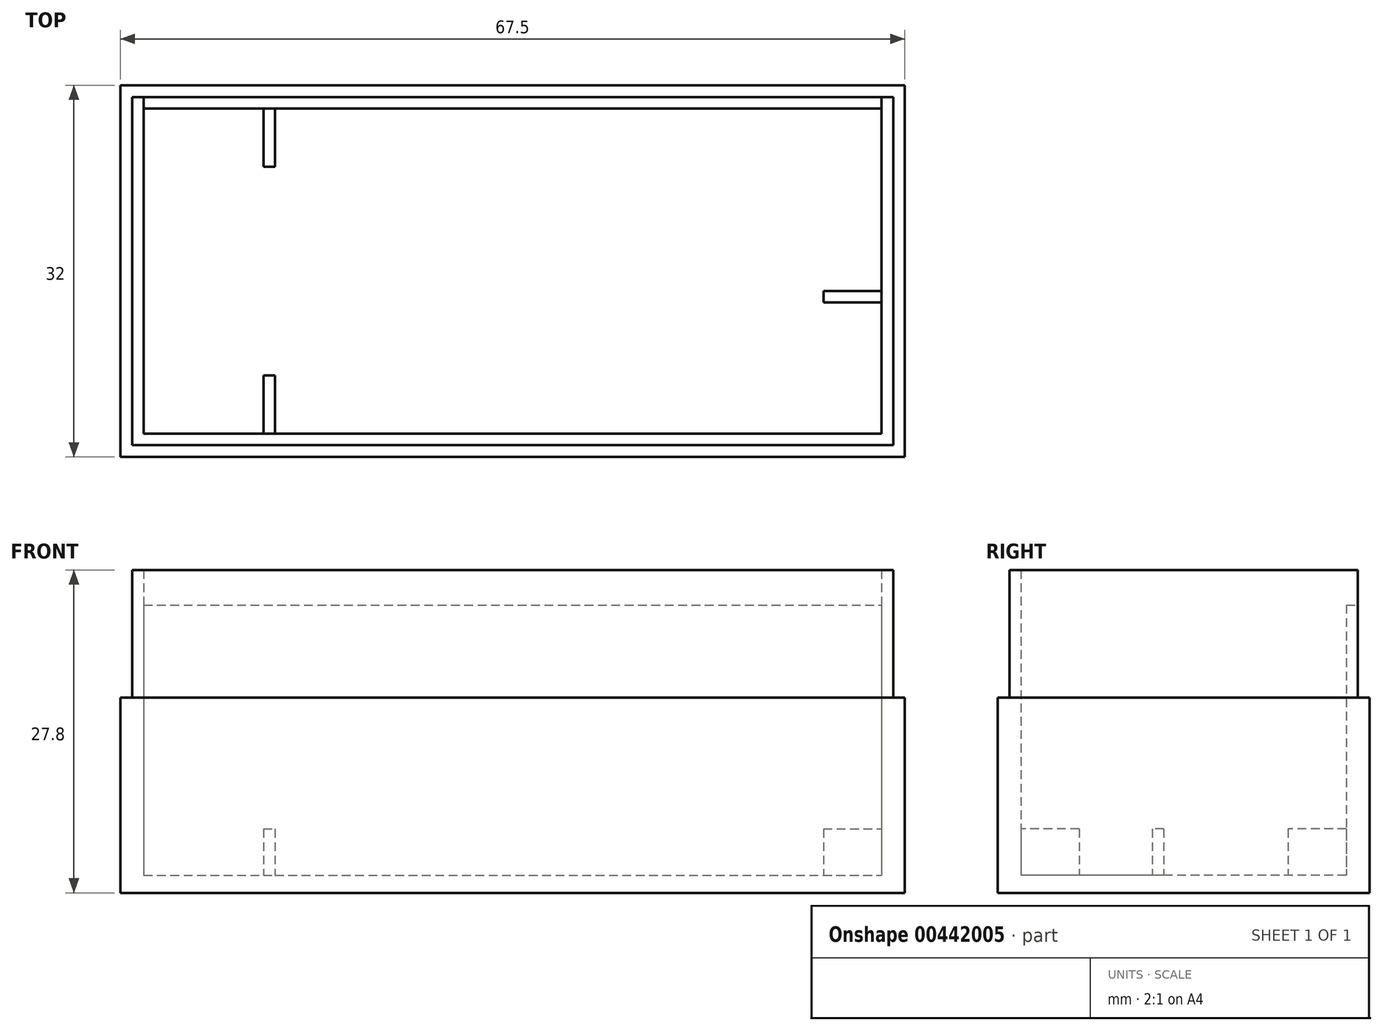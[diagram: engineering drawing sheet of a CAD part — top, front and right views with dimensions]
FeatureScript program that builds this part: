
annotation { "Feature Type Name" : "Feature", "Feature Type Description" : "" }
export const myFeature = defineFeature(function(context is Context, id is Id, definition is map)
    precondition{}
    {
        {
            var Q0;
            Q0=qCreatedBy(makeId("Top.planeOp"),FACE);
            var sketch = newSketch(context, id + "F0", { "sketchPlane" : qUnion([Q0])});
            skLineSegment(sketch, "E0.bottom", {"start": v(0, 0) * mm, "end": v(67.5, 0) * mm});
            skLineSegment(sketch, "E0.top", {"start": v(0, 32) * mm, "end": v(67.5, 32) * mm});
            skLineSegment(sketch, "E0.left", {"start": v(0, 0) * mm, "end": v(0, 32) * mm});
            skLineSegment(sketch, "E0.right", {"start": v(67.5, 0) * mm, "end": v(67.5, 32) * mm});
            skSolve(sketch);
        }
        {
            var Q0;
            Q0 = qSketchRegion(id + "F0", true);
            extrude(context, id + "F1", {"entities" : qUnion([Q0]), "depth" : 1.5 * mm});
        }
        {
            var Q0;
            Q0=makeQuery(id+"F1.opExtrude","CAP_FACE",FACE,{"disambiguationData":[OSD([sQuery(id+"F0.wireOp",EDGE,"E0.bottom"),sQuery(id+"F0.wireOp",EDGE,"E0.top"),sQuery(id+"F0.wireOp",EDGE,"E0.left"),sQuery(id+"F0.wireOp",EDGE,"E0.right")])],"isStart":false});
            var sketch = newSketch(context, id + "F2", { "sketchPlane" : qUnion([Q0])});
            skLineSegment(sketch, "E1.bottom", {"start": v(0, 32) * mm, "end": v(67.5, 32) * mm});
            skLineSegment(sketch, "E1.top", {"start": v(0, 0) * mm, "end": v(67.5, 0) * mm});
            skLineSegment(sketch, "E1.left", {"start": v(0, 32) * mm, "end": v(0, 0) * mm});
            skLineSegment(sketch, "E1.right", {"start": v(67.5, 32) * mm, "end": v(67.5, 0) * mm});
            skLineSegment(sketch, "E2.bottom", {"start": v(2, 30) * mm, "end": v(65.5, 30) * mm});
            skLineSegment(sketch, "E2.top", {"start": v(2, 2) * mm, "end": v(65.5, 2) * mm});
            skLineSegment(sketch, "E2.left", {"start": v(2, 30) * mm, "end": v(2, 2) * mm});
            skLineSegment(sketch, "E2.right", {"start": v(65.5, 30) * mm, "end": v(65.5, 2) * mm});
            skSolve(sketch);
        }
        {
            var Q0;
            Q0 = qSketchRegion(id + "F2", true);
            extrude(context, id + "F3", {"entities" : qUnion([Q0]), "operationType" : NewBodyOperationType.ADD, "depth" : 26.3 * mm});
        }
        {
            var Q0;
            Q0=makeQuery(id+"F3.opExtrude","CAP_FACE",FACE,{"disambiguationData":[OSD([sQuery(id+"F2.wireOp",EDGE,"E1.bottom"),sQuery(id+"F2.wireOp",EDGE,"E1.top"),sQuery(id+"F2.wireOp",EDGE,"E1.left"),sQuery(id+"F2.wireOp",EDGE,"E1.right"),sQuery(id+"F2.wireOp",EDGE,"E2.bottom"),sQuery(id+"F2.wireOp",EDGE,"E2.top"),sQuery(id+"F2.wireOp",EDGE,"E2.left"),sQuery(id+"F2.wireOp",EDGE,"E2.right")])],"isStart":false});
            var sketch = newSketch(context, id + "F4", { "sketchPlane" : qUnion([Q0])});
            skLineSegment(sketch, "E3.bottom", {"start": v(2, 30) * mm, "end": v(65.5, 30) * mm});
            skLineSegment(sketch, "E3.top", {"start": v(2, 32) * mm, "end": v(65.5, 32) * mm});
            skLineSegment(sketch, "E3.left", {"start": v(2, 30) * mm, "end": v(2, 32) * mm});
            skLineSegment(sketch, "E3.right", {"start": v(65.5, 30) * mm, "end": v(65.5, 32) * mm});
            skSolve(sketch);
        }
        {
            var Q0;
            Q0 = qSketchRegion(id + "F4", true);
            extrude(context, id + "F5", {"entities" : qUnion([Q0]), "operationType" : NewBodyOperationType.REMOVE, "oppositeDirection" : true, "depth" : 3 * mm});
        }
        {
            var Q0;
            Q0=makeQuery(id+"F3.opExtrude","CAP_FACE",FACE,{"disambiguationData":[OSD([sQuery(id+"F2.wireOp",EDGE,"E1.bottom"),sQuery(id+"F2.wireOp",EDGE,"E1.top"),sQuery(id+"F2.wireOp",EDGE,"E1.left"),sQuery(id+"F2.wireOp",EDGE,"E1.right"),sQuery(id+"F2.wireOp",EDGE,"E2.bottom"),sQuery(id+"F2.wireOp",EDGE,"E2.top"),sQuery(id+"F2.wireOp",EDGE,"E2.left"),sQuery(id+"F2.wireOp",EDGE,"E2.right")])],"isStart":false});
            var sketch = newSketch(context, id + "F6", { "sketchPlane" : qUnion([Q0])});
            skLineSegment(sketch, "E4.bottom", {"start": v(0, 32) * mm, "end": v(67.5, 32) * mm});
            skLineSegment(sketch, "E4.top", {"start": v(0, 0) * mm, "end": v(67.5, 0) * mm});
            skLineSegment(sketch, "E4.left", {"start": v(0, 32) * mm, "end": v(0, 0) * mm});
            skLineSegment(sketch, "E4.right", {"start": v(67.5, 32) * mm, "end": v(67.5, 0) * mm});
            skLineSegment(sketch, "E5.bottom", {"start": v(1, 31) * mm, "end": v(66.5, 31) * mm});
            skLineSegment(sketch, "E5.top", {"start": v(1, 1) * mm, "end": v(66.5, 1) * mm});
            skLineSegment(sketch, "E5.left", {"start": v(1, 31) * mm, "end": v(1, 1) * mm});
            skLineSegment(sketch, "E5.right", {"start": v(66.5, 31) * mm, "end": v(66.5, 1) * mm});
            skSolve(sketch);
        }
        {
            var Q0;
            Q0 = qSketchRegion(id + "F6", true);
            extrude(context, id + "F7", {"entities" : qUnion([Q0]), "operationType" : NewBodyOperationType.REMOVE, "oppositeDirection" : true, "depth" : 11 * mm});
        }
        {
            var Q0;
            Q0=makeQuery(id+"F1.opExtrude","CAP_FACE",FACE,{"disambiguationData":[OSD([sQuery(id+"F0.wireOp",EDGE,"E0.bottom"),sQuery(id+"F0.wireOp",EDGE,"E0.top"),sQuery(id+"F0.wireOp",EDGE,"E0.left"),sQuery(id+"F0.wireOp",EDGE,"E0.right")])],"isStart":false});
            var sketch = newSketch(context, id + "F8", { "sketchPlane" : qUnion([Q0])});
            skLineSegment(sketch, "E6.bottom", {"start": v(60.5, 14.3) * mm, "end": v(65.5, 14.3) * mm});
            skLineSegment(sketch, "E6.top", {"start": v(60.5, 13.3) * mm, "end": v(65.5, 13.3) * mm});
            skLineSegment(sketch, "E6.left", {"start": v(60.5, 14.3) * mm, "end": v(60.5, 13.3) * mm});
            skLineSegment(sketch, "E6.right", {"start": v(65.5, 14.3) * mm, "end": v(65.5, 13.3) * mm});
            skLineSegment(sketch, "E7.bottom", {"start": v(12.3, 30) * mm, "end": v(13.3, 30) * mm});
            skLineSegment(sketch, "E7.top", {"start": v(12.3, 25) * mm, "end": v(13.3, 25) * mm});
            skLineSegment(sketch, "E7.left", {"start": v(12.3, 30) * mm, "end": v(12.3, 25) * mm});
            skLineSegment(sketch, "E7.right", {"start": v(13.3, 30) * mm, "end": v(13.3, 25) * mm});
            skLineSegment(sketch, "E8.bottom", {"start": v(12.3, 7) * mm, "end": v(13.3, 7) * mm});
            skLineSegment(sketch, "E8.top", {"start": v(12.3, 2) * mm, "end": v(13.3, 2) * mm});
            skLineSegment(sketch, "E8.left", {"start": v(12.3, 7) * mm, "end": v(12.3, 2) * mm});
            skLineSegment(sketch, "E8.right", {"start": v(13.3, 7) * mm, "end": v(13.3, 2) * mm});
            skSolve(sketch);
        }
        {
            var Q0;
            Q0 = qSketchRegion(id + "F8", true);
            extrude(context, id + "F9", {"entities" : qUnion([Q0]), "operationType" : NewBodyOperationType.ADD, "depth" : 4 * mm});
        }
    });
